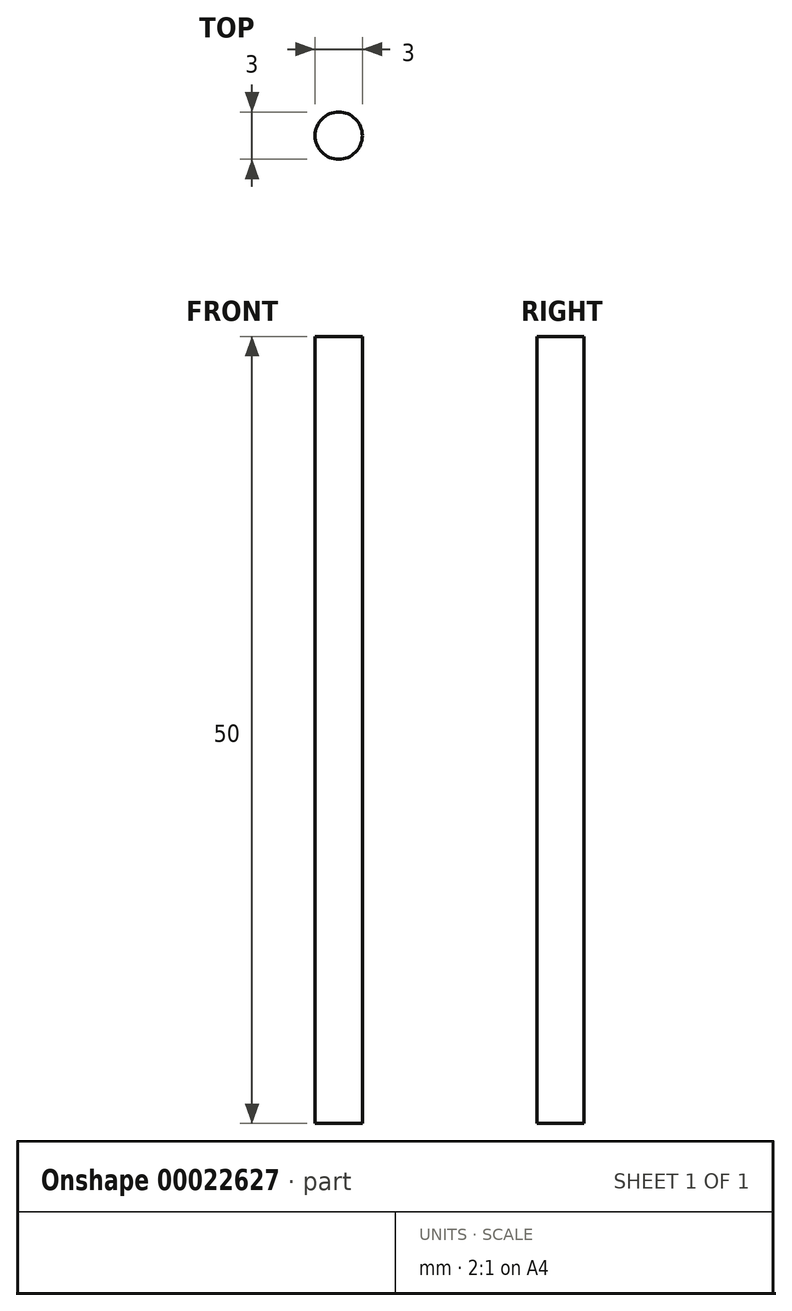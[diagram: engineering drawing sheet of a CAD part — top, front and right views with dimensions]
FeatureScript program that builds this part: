
annotation { "Feature Type Name" : "Feature", "Feature Type Description" : "" }
export const myFeature = defineFeature(function(context is Context, id is Id, definition is map)
    precondition{}
    {
        {
            var Q0;
            Q0=qCreatedBy(makeId("Front.planeOp"),FACE);
            var sketch = newSketch(context, id + "F0", { "sketchPlane" : qUnion([Q0])});
            skLineSegment(sketch, "E0.bottom", {"start": v(-1.5, 45.6) * mm, "end": v(0, 45.6) * mm});
            skLineSegment(sketch, "E0.top", {"start": v(-1.5, -4.4) * mm, "end": v(0, -4.4) * mm});
            skLineSegment(sketch, "E0.left", {"start": v(-1.5, 45.6) * mm, "end": v(-1.5, -4.4) * mm});
            skLineSegment(sketch, "E0.right", {"start": v(0, 45.6) * mm, "end": v(0, -4.4) * mm});
            skSolve(sketch);
        }
        {
            var Q0;
            Q0=makeQuery(id+"F0.imprint","IMPRINT",FACE,{"disambiguationData":[TD([[makeQuery(id+"F0.imprint","IMPRINT",EDGE,{"derivedFrom":sQuery(id+"F0.wireOp",EDGE,"E0.bottom")}),-1.0]])]});
            var Q1;
            Q1=sQuery(id+"F0.wireOp",EDGE,"E0.left");
            revolve(context, id + "F1", {"entities" : qUnion([Q0]), "axis" : qUnion([Q1]), "revolveType" : RevolveType.FULL});
        }
    });
